# Revit family: LEGRAND_TOMAS SIN ENCLAVAMIENTO_EMPOTRADAS_IP66_400
name_source: partatom
category: Installations électriques
revit_build: Autodesk Revit 2018 (Build: 20170223_1515(x64)
units: mm (PartAtom-declared; Revit-internal decimal feet)

## family parameters
Conserver l'orientation des annotations = Non
Cote de connecteur circulaire = Utiliser le diamètre
Couper avec des vides une fois chargée = Non
Hôte = Face
Partagée = Non
Point de calcul de pièce = Non
Type d'élément = Normal

## types (10) — shared parameters
Condiciones Generales de Uso = https://export.legrand.com
Description = Toma AL estándar internacional para montaje empotrado o en superficie con accesorio permite la alimentación de aparatos de potencia
Elévation par défaut = 1000 mm
Estándar CEI o NFC = CEI
Fabricant = Legrand
Temperatura maxima de instalación = 40°C
Temperatura maxima de uso = 100°C
Temperatura minima de instalación = -20°C
Temperatura minima de uso = -50°C
Tension V = 400 V  50/60 Hz rojo
clase de protección IP = IP66/67-55
color característico = rojo
instalación de empotrar E o de superficie S = empotrar y superficie
materia de la caja = plástico
resistencia a los choques IK = 09
sin halogeno = Non
tipo de enclavamiento = conexión por tonillo

## per-type parameters (varying)
| type | Dia bouchon | Modèle | RAY BOUCHON | Ray | altura mm | ancho mm | dIA | distancia de fijación horizontal mm | distancia de fijación vertical mm | h1 | intensidad A | numero de polos | posición de la tierra h | profundidad de empotrar mm | profundidad mm |
| base para cuadro Hypra   IP66/67-55   16 A   380/415 V   3P+T   plast | 79 mm | 051130 | 40 mm | 26 mm | 84 mm | 74 mm | 53 mm | 60 mm | 70 mm | 50 mm  [stored 0.164042 ft] | 16 A | 4 | 6 | 41 mm | 89 mm  [stored 0.291995 ft] |
| base para cuadro Hypra   IP66/67-55   16 A   380/415 V   3P+N+T   plast | 82 mm | 051131 | 41 mm | 27 mm | 84 mm | 80 mm | 55 mm | 60 mm | 70 mm | 50 mm  [stored 0.164042 ft] | 16 A | 6 | 6 | 42 mm  [stored 0.137795 ft] | 92 mm |
| base para cuadro entreejes unificados Hypra  IP66/67-55  16 A   380/415 V   3P+T   plast | 84 mm | 051150 | 42 mm  [stored 0.137795 ft] | 28 mm | 84 mm | 84 mm | 56 mm | 70 mm | 70 mm | 50 mm  [stored 0.164042 ft] | 16 A | 4 | 6 | 43 mm | 84 mm |
| base para cuadro entreejes unificados Hypra  IP66/67-55  16 A  380/415 V   3P+N+T  plast | 84 mm | 051151 | 42 mm  [stored 0.137795 ft] | 28 mm | 84 mm | 84 mm | 56 mm | 70 mm | 70 mm | 50 mm  [stored 0.164042 ft] | 16 A | 5 | 6 | 43 mm | 84 mm |
| base para cuadro entreejes unificados Hypra  IP66/67-55  32 A   380 415 V   3P+T   plast | 89 mm  [stored 0.291995 ft] | 053050 | 45 mm | 30 mm  [stored 0.0984252 ft] | 94 mm | 84 mm | 59 mm | 70 mm | 70 mm | 56 mm | 32 A | 4 | 6 | 54 mm | 104 mm |
| base para cuadro entreejes unificados Hypra  IP66/67-55  32 A  380/415 V   3P+N+T  plast | 89 mm  [stored 0.291995 ft] | 053051 | 45 mm | 30 mm  [stored 0.0984252 ft] | 94 mm | 84 mm | 59 mm | 70 mm | 70 mm | 56 mm | 32 A | 5 | 6 | 54 mm | 105 mm  [stored 0.344488 ft] |
| base para cuadro Hypra  IP66/67-55   63A   380 415 V   3P+T   plast | 106 mm | 059427 | 53 mm | 35 mm | 106 mm | 106 mm | 71 mm | 77 mm | 85 mm | 64 mm | 63 A | 4 | 9 | 85 mm | 164 mm |
| base para cuadro Hypra  IP66/67-55   63A   380 415 V   3P+N+T   plast | 106 mm | 059428 | 53 mm | 35 mm | 106 mm | 106 mm | 71 mm | 77 mm | 85 mm | 64 mm | 63 A | 4 | 9 | 85 mm | 164 mm |
| base para cuadro Hypra  IP66/67-55   125A   380 415 V  3P+T   plast | 146 mm  [stored 0.479003 ft] | 059512 | 73 mm  [stored 0.239501 ft] | 49 mm | 146 mm  [stored 0.479003 ft] | 146 mm  [stored 0.479003 ft] | 97 mm | 124 mm | 124 mm | 88 mm | 125 A | 4 | 6 | 84 mm | 180 mm |
| base para cuadro Hypra  IP66/67-55   125A   380 415 V   3P+N+T   plast | 146 mm  [stored 0.479003 ft] | 059513 | 73 mm  [stored 0.239501 ft] | 49 mm | 146 mm  [stored 0.479003 ft] | 146 mm  [stored 0.479003 ft] | 97 mm | 124 mm | 124 mm | 88 mm | 125 A | 5 | 6 | 84 mm | 180 mm |

note: [stored X ft] marks values corroborated as IEEE doubles in the binary element streams (Revit-internal decimal feet)
